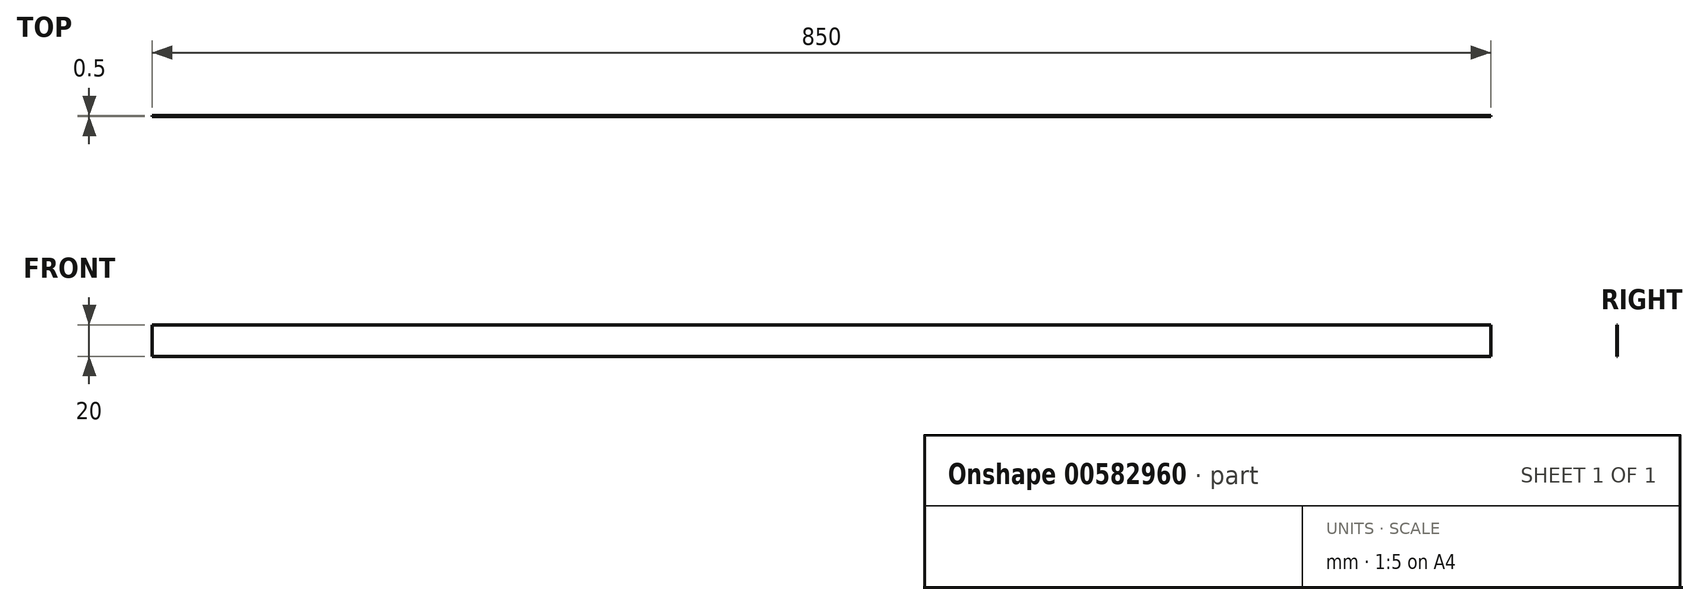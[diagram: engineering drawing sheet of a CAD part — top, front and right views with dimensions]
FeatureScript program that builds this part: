
annotation { "Feature Type Name" : "Feature", "Feature Type Description" : "" }
export const myFeature = defineFeature(function(context is Context, id is Id, definition is map)
    precondition{}
    {
        {
            var Q0;
            Q0=qCreatedBy(makeId("Front.planeOp"),FACE);
            var sketch = newSketch(context, id + "F0", { "sketchPlane" : qUnion([Q0])});
            skLineSegment(sketch, "E0", {"start": v(0, 34.2) * mm, "end": v(0, -45.96) * mm, "construction": true});
            skLineSegment(sketch, "E1.bottom", {"start": v(-425, 10) * mm, "end": v(425, 10) * mm});
            skLineSegment(sketch, "E1.top", {"start": v(-425, -10) * mm, "end": v(425, -10) * mm});
            skLineSegment(sketch, "E1.left", {"start": v(-425, 10) * mm, "end": v(-425, -10) * mm});
            skLineSegment(sketch, "E1.right", {"start": v(425, 10) * mm, "end": v(425, -10) * mm});
            skSolve(sketch);
        }
        {
            var Q0;
            Q0=qSketchRegion(id+"F0",true);
            extrude(context, id + "F1", {"entities" : qUnion([Q0]), "depth" : 0.5 * mm, "offsetDistance" : 25 * mm});
        }
    });
